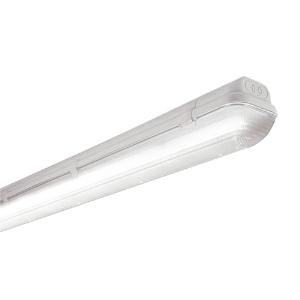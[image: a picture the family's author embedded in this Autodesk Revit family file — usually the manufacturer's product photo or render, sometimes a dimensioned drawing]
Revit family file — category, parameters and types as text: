
# Revit family: 3f_filippi_-_3f_linda_basic_3f_filippi_-_58764_-_3f_linda_led_basic_1x23w_l1570
name_source: partatom
category: Lighting Fixtures
units: mm (PartAtom-declared; Revit-internal decimal feet)

## family parameters
Cut with Voids When Loaded = No
Host = Face
Light Source = No
Part Type = Normal
Room Calculation Point = No
Round Connector Dimension = Use Diameter
Shared = No

## types (1)
- 3F Filippi - 3F Linda Basic (1 x LED, 3548 lm, 23 W, 4000 K)
    Apparent Load = 23 VA
    Approval mark = CE
    CIE Flux Codes = 44 77 94 97 100
    Color Rendering = 80
    Color Temperature = 4000 K
    Control Gear = Electronic ballast
    Default Elevation = 1800 mm
    Description = ILLUMINOTECHNICAL
Luminous efficiency 100% (DLOR 97%, ULOR 3%).
Initial luminous flux of the luminaire 3548 lm.
Controlled direct symmetric distribution.
Installation Interdistance Transv.D = 1.77 x hu - Long.D = 1.17 x hu.
Tabular UGR (CIE 117 - 4H-8H; S=0.25H; 70/50/20): RUG 20.8 - 21.8.
Beam angle: 109° - 64°.
Luminous efficacy 154 lm/W.
Lifetime (L92/B10): 30000 h. (tq+25°C)
Lifetime (L85/B10): 50000 h. (tq+25°C)
Lifetime (L75/B10): 80000 h. (tq+25°C)
Lifetime (L70/B10): 100000 h. (tq+25°C)
Lifetime (L75/B10): 50000 h. (tq+40°C)
Sudden decreased luminous flux after 50000 hours: 0% (C0).
Photobiological safety in compliance with IEC/TR 62778: RG0 risk exempt, (IEC 62471).
In compliance with IEC/EN 62722-2-1 - IEC/EN 62717 standards.

SOURCE
Linear LED module 23W/840.
Energy efficiency class (UE 2019/2020 - UE 2019/2015): D.
CIE 13.3 Colour rendering index: CRI >80 (R9 <50%).
IES TM-30 Fidelity Index: Rf = 84 Rg = 95.
CCT nominal colour temperature 4000 K.
Colour initial tolerance (MacAdam): SDCM 3.

MECHANICAL
Self-extinguishing V2 polycarbonate housing, injection moulded, RAL 7035 grey.
Ecologic anti-aging injected sealing gasket.
Diffuser in self-extinguishing V2 polycarbonate, photo-engraved interior, UV stabilised, injection moulded with smooth outer surface, tamper-proof opening.
Gear-holder reflector in hot-dip galvanised steel, painted with white polyester base.
Snug fit snap-lock clips for diffuser mounting, in polycarbonate.
Fixing brackets in stainless steel.
Possibility for technicians to access the interior of the luminaire.
Luminaire with limited surface temperature. - D - (EN 60598-2-24)
Dimensions: 1570x100 mm, height 100 mm. Weight 2.33 kg.
IP66 protection degree.
Mechanical strength to impacts IK10 (20 joule).
Glow-wire test resistance 850°C.

ELECTRICAL
Halogen Free electronic wiring 230V-50/60Hz, power factor 0.90, THD <25%, constant output current, SELV, class I, 1 driver.
Power of the luminaire 23 W.
ENEC - CE.
SAFE FLICKER: PstLM=<1 and SVM=<0.4 (IEC TR 61547-1 and IEC TR 63158), to ensure a more comfortable and safe light.
Luminaire compliant with EN 60598-2-22 for power supply from a centralised emergency system CPSS (Central Power Supply System), not incorporated in the luminaire - high risk areas excluded. The default power and flux are 100% in AC and 100% in DC.
Ambient temperature from -20°C to +40°C.
Temperature class T6 max 85°C.
Relative humidity UR: <85%.

INSTALLATION
Ceiling / Suspended / Wall.
All accessories dedicated to this product are available on the Catalog and on our website www.3F-Filippi.com.

APPLICATIONS
Suitable product for food production plants (HACCP), IFS (Food Version 6), BRC (GSFS Food Version 7).
Dry, dusty indoor environments, subject to occasional water splashes.
Virtually shatterproof polycarbonate compatibly with the fumes / atmospheres that compromise the elasticity of plastic materials.
Not suitable for installation on surfaces subject to important vibrations, exposed to weather conditions, on ropes or poles.
Suitable for illumination of public car parks and parking grounds referred to DIN 67528:2018-04.

WARNING
Fixture not suitable for cold stores with an ambient temperature <0°C and/or relative humidity >85%.
Luminaire designed for disposal/recycling at end-of-life.
Replaceable (LED only) light source by a professional. Replaceable control gear by a professional.
    Height = 100 mm  [stored 0.328084 ft]
    Lamp = 1 x LED
    Lamp Light Flux = 3548 lm
    Lamp Power = 23 W
    Lamp count = 1
    Length = 1570 mm
    Lifetime = 50000 h
    Luminous efficacy = 154 lm/W
    Manufacturer = 3F Filippi
    ModVariant = No
    Model = 3F Filippi - 58764 - 3F Linda LED Basic 1x23W L1570
    Mounting Place = Ceiling
    Mounting Type = Pendant
    Number of Poles = 1
    OnlyDefault = Yes
    Power Factor = 1
    Product Name = 3F Filippi - 3F Linda Basic
    Product group = pendant luminaire
    ProductGroupID = 9
    Protection Class = Protection class I
    Protection Degree = IP 66
    RLX_Detail_Level = 1
    RLX_Emergency_Light_Flux = 0 lm
    RLX_Emergency_Type = 0
    RLX_Emergency_Type_DB = No
    RlxData = <blob elided: 58761 chars, md5=7d8aec97>
    Socket = socket
    Standby Power = 0 W
    System Light Flux = 3548 lm
    System Power = 23 W
    Type Comments = Product without accessories
    Type Image = 3ffilippi_3f_linda_led_basic_1x.jpg
    URL = http://relux.com
    VarID = ---
    Voltage = 0 V
    Weight = 0.00 kg
    Width = 100 mm  [stored 0.328084 ft]

note: [stored X ft] marks values corroborated as IEEE doubles in the binary element streams (Revit-internal decimal feet)

## geometry (parser evidence)
native form markers: Blend x4, Sweep x11
no freeform markers — native parametric forms only
